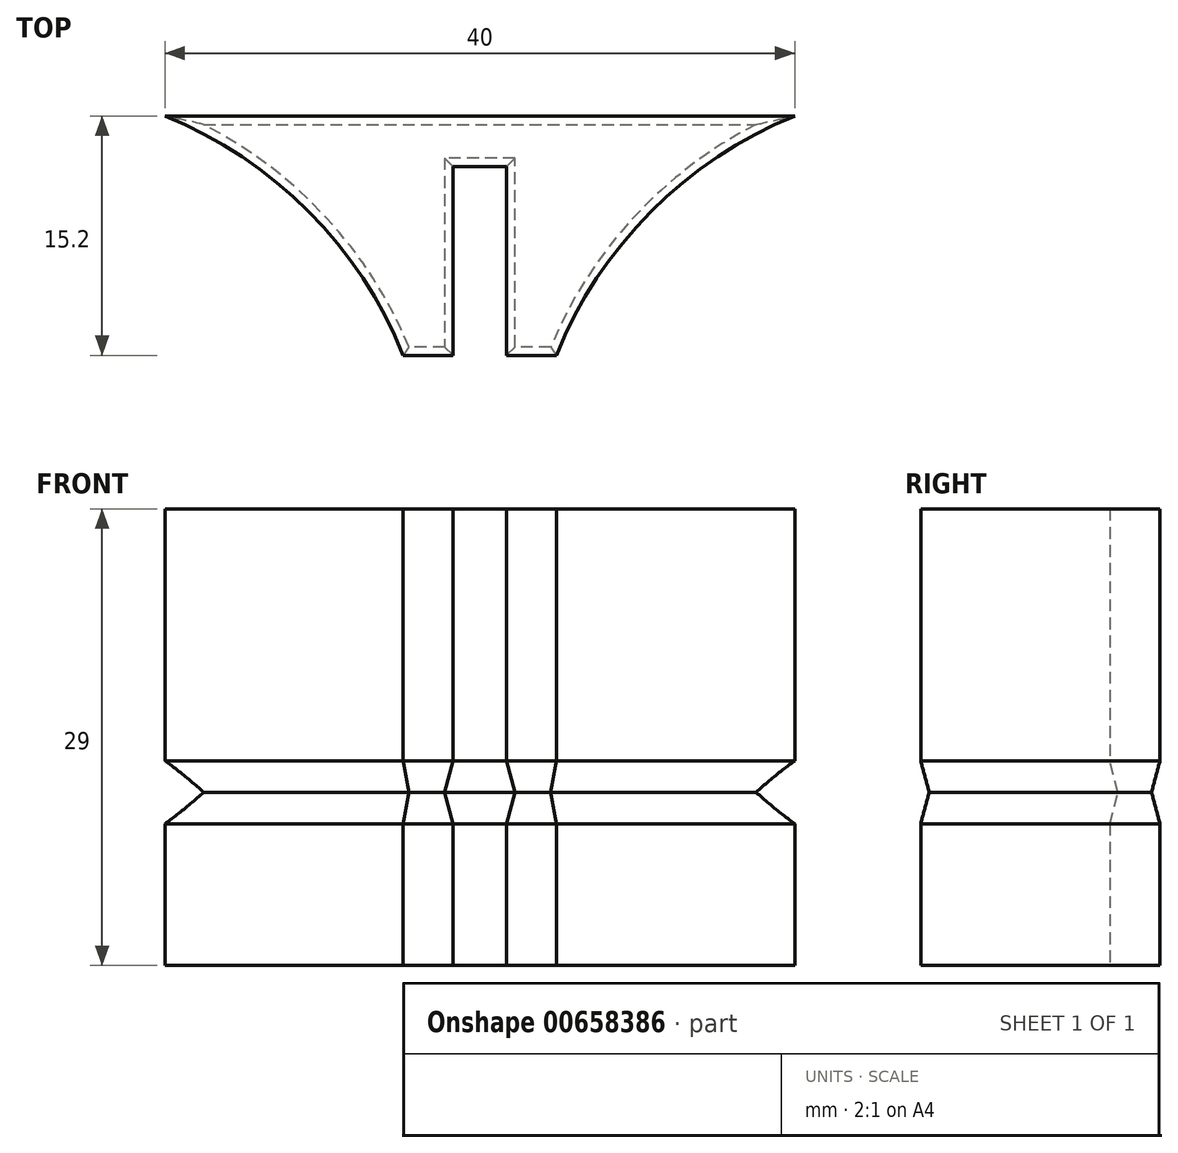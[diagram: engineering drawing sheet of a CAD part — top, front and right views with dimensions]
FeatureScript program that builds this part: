
annotation { "Feature Type Name" : "Feature", "Feature Type Description" : "" }
export const myFeature = defineFeature(function(context is Context, id is Id, definition is map)
    precondition{}
    {
        {
            var Q0;
            Q0=qCreatedBy(makeId("Top.planeOp"),FACE);
            var sketch = newSketch(context, id + "F0", { "sketchPlane" : qUnion([Q0])});
            skLineSegment(sketch, "E0.bottom", {"start": v(-1.7, 6) * mm, "end": v(1.7, 6) * mm});
            skLineSegment(sketch, "E0.top", {"start": v(-1.7, -6) * mm, "end": v(1.7, -6) * mm});
            skLineSegment(sketch, "E0.left", {"start": v(-1.7, 6) * mm, "end": v(-1.7, -6) * mm});
            skLineSegment(sketch, "E0.right", {"start": v(1.7, 6) * mm, "end": v(1.7, -6) * mm});
            skPoint(sketch, "E0.middle", {"position": v(0, 0) * mm});
            skLineSegment(sketch, "E1", {"start": v(-1.7, -6) * mm, "end": v(-4.86, -6) * mm});
            skArc(sketch, "E2", {"start": v(-4.86, -6) * mm, "mid": v(-10.88, 3.15) * mm, "end": v(-20, 9.2) * mm});
            skLineSegment(sketch, "E3", {"start": v(-20, 9.2) * mm, "end": v(0, 9.2) * mm});
            skLineSegment(sketch, "E4", {"start": v(0, 0) * mm, "end": v(0, -2.54) * mm});
            skLineSegment(sketch, "E5.MirrorCS", {"start": v(20, 9.2) * mm, "end": v(0, 9.2) * mm});
            skArc(sketch, "E6.MirrorCS", {"start": v(4.86, -6) * mm, "mid": v(10.88, 3.15) * mm, "end": v(20, 9.2) * mm});
            skLineSegment(sketch, "E7.MirrorCS", {"start": v(1.7, -6) * mm, "end": v(4.86, -6) * mm});
            skSolve(sketch);
        }
        {
            var Q0;
            Q0=makeQuery(id+"F0.imprint","IMPRINT",FACE,{"disambiguationData":[TD([[makeQuery(id+"F0.imprint","IMPRINT",EDGE,{"derivedFrom":sQuery(id+"F0.wireOp",EDGE,"E0.bottom")}),1.0]])]});
            extrude(context, id + "F1", {"entities" : qUnion([Q0]), "depth" : 9 * mm, "offsetDistance" : 25 * mm});
        }
        {
            var Q0;
            Q0=makeQuery(id+"F1.opExtrude","CAP_FACE",FACE,{"disambiguationData":[OSD([sQuery(id+"F0.wireOp",EDGE,"E0.bottom"),sQuery(id+"F0.wireOp",EDGE,"E0.left"),sQuery(id+"F0.wireOp",EDGE,"E0.right"),sQuery(id+"F0.wireOp",EDGE,"E1"),sQuery(id+"F0.wireOp",EDGE,"E2"),sQuery(id+"F0.wireOp",EDGE,"E3"),sQuery(id+"F0.wireOp",EDGE,"E5.MirrorCS"),sQuery(id+"F0.wireOp",EDGE,"E6.MirrorCS"),sQuery(id+"F0.wireOp",EDGE,"E7.MirrorCS")])],"isStart":false});
            var sketch = newSketch(context, id + "F2", { "sketchPlane" : qUnion([Q0])});
            skSolve(sketch);
        }
        {
            var Q0;
            Q0=makeQuery(id+"F2.imprint","IMPRINT",FACE,{"disambiguationData":[TD([[makeQuery(id+"F2.imprint","IMPRINT",EDGE,{"derivedFrom":makeQuery(id+"F1.opExtrude","CAP_EDGE",EDGE,{"disambiguationData":[OSD([sQuery(id+"F0.wireOp",EDGE,"E0.bottom")])],"isStart":false})}),1.0]])]});
            extrude(context, id + "F3", {"entities" : qUnion([Q0]), "operationType" : NewBodyOperationType.ADD, "depth" : 2 * mm, "offsetDistance" : 25 * mm, "hasDraft" : true, "draftAngle" : 15 * degree, "draftPullDirection" : true});
        }
        {
            var Q0;
            Q0=makeQuery(id+"F3.opExtrude","CAP_FACE",FACE,{"disambiguationData":[OSD([sQuery(id+"F0.wireOp",EDGE,"E0.bottom"),sQuery(id+"F0.wireOp",EDGE,"E0.left"),sQuery(id+"F0.wireOp",EDGE,"E0.right"),sQuery(id+"F0.wireOp",EDGE,"E1"),sQuery(id+"F0.wireOp",EDGE,"E2"),sQuery(id+"F0.wireOp",EDGE,"E3"),sQuery(id+"F0.wireOp",EDGE,"E5.MirrorCS"),sQuery(id+"F0.wireOp",EDGE,"E6.MirrorCS"),sQuery(id+"F0.wireOp",EDGE,"E7.MirrorCS")])],"isStart":false});
            extrude(context, id + "F4", {"entities" : qUnion([Q0]), "operationType" : NewBodyOperationType.ADD, "depth" : 2 * mm, "offsetDistance" : 25 * mm, "hasDraft" : true, "draftAngle" : 15 * degree});
        }
        {
            var Q0;
            Q0=makeQuery(id+"F4.opExtrude","CAP_FACE",FACE,{"disambiguationData":[OSD([sQuery(id+"F0.wireOp",EDGE,"E0.bottom"),sQuery(id+"F0.wireOp",EDGE,"E0.left"),sQuery(id+"F0.wireOp",EDGE,"E0.right"),sQuery(id+"F0.wireOp",EDGE,"E1"),sQuery(id+"F0.wireOp",EDGE,"E2"),sQuery(id+"F0.wireOp",EDGE,"E3"),sQuery(id+"F0.wireOp",EDGE,"E5.MirrorCS"),sQuery(id+"F0.wireOp",EDGE,"E6.MirrorCS"),sQuery(id+"F0.wireOp",EDGE,"E7.MirrorCS")])],"isStart":false});
            extrude(context, id + "F5", {"entities" : qUnion([Q0]), "operationType" : NewBodyOperationType.ADD, "depth" : 16 * mm, "offsetDistance" : 25 * mm});
        }
    });
